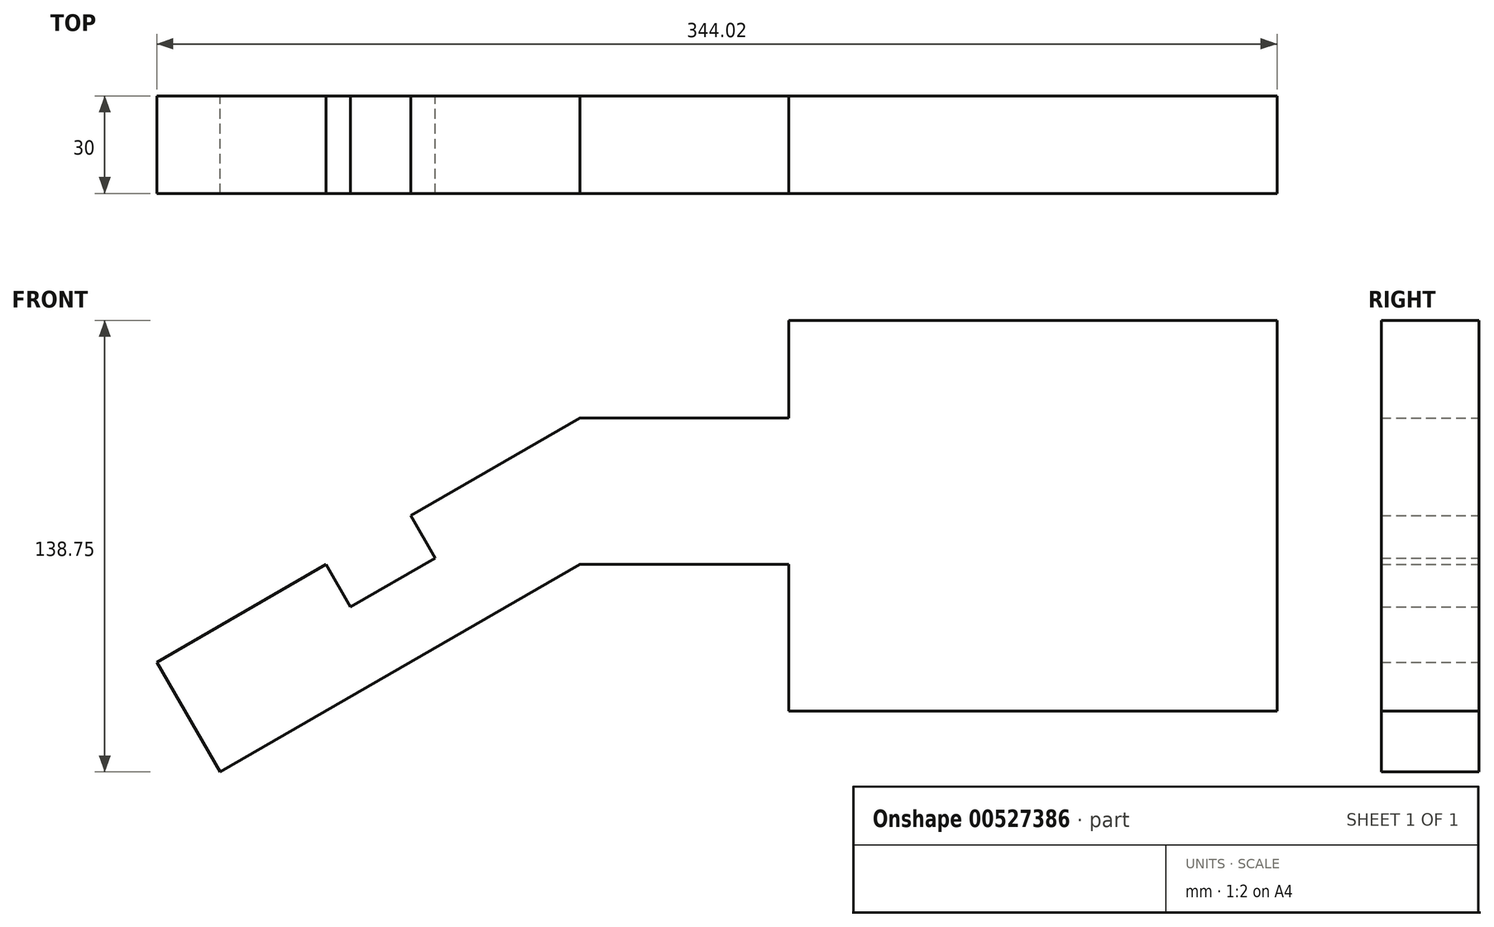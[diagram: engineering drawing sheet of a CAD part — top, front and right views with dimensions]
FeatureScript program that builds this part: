
annotation { "Feature Type Name" : "Feature", "Feature Type Description" : "" }
export const myFeature = defineFeature(function(context is Context, id is Id, definition is map)
    precondition{}
    {
        {
            var Q0;
            Q0=qCreatedBy(makeId("Front.planeOp"),FACE);
            var sketch = newSketch(context, id + "F0", { "sketchPlane" : qUnion([Q0])});
            skLineSegment(sketch, "E0", {"start": v(-129.83, -10.53) * mm, "end": v(-77.86, 19.47) * mm});
            skLineSegment(sketch, "E1", {"start": v(-77.86, 19.47) * mm, "end": v(-70.36, 6.48) * mm});
            skLineSegment(sketch, "E2", {"start": v(-70.36, 6.48) * mm, "end": v(-44.38, 21.48) * mm});
            skLineSegment(sketch, "E3", {"start": v(-44.38, 21.48) * mm, "end": v(-51.88, 34.47) * mm});
            skLineSegment(sketch, "E4", {"start": v(-51.88, 34.47) * mm, "end": v(0.08, 64.47) * mm});
            skLineSegment(sketch, "E5", {"start": v(0.08, 64.47) * mm, "end": v(120.08, 64.47) * mm});
            skLineSegment(sketch, "E6", {"start": v(120.08, 64.47) * mm, "end": v(120.08, 19.47) * mm});
            skLineSegment(sketch, "E7", {"start": v(120.08, 19.47) * mm, "end": v(0.08, 19.47) * mm});
            skLineSegment(sketch, "E8", {"start": v(0.08, 19.47) * mm, "end": v(-110.34, -44.28) * mm});
            skLineSegment(sketch, "E9", {"start": v(64.2, 94.47) * mm, "end": v(64.2, 64.47) * mm});
            skLineSegment(sketch, "E10", {"start": v(64.2, 19.47) * mm, "end": v(64.2, -25.53) * mm});
            skLineSegment(sketch, "E11", {"start": v(64.2, -25.53) * mm, "end": v(214.2, -25.53) * mm});
            skLineSegment(sketch, "E12", {"start": v(214.2, -25.53) * mm, "end": v(214.2, 94.47) * mm});
            skLineSegment(sketch, "E13", {"start": v(214.2, 94.47) * mm, "end": v(64.2, 94.47) * mm});
            skLineSegment(sketch, "E14", {"start": v(-129.83, -10.53) * mm, "end": v(-110.34, -44.28) * mm});
            skSolve(sketch);
        }
        {
            var Q0;
            Q0 = qSketchRegion(id + "F0", true);
            extrude(context, id + "F1", {"entities" : qUnion([Q0]), "depth" : 30 * mm, "offsetDistance" : 25 * mm});
        }
    });
